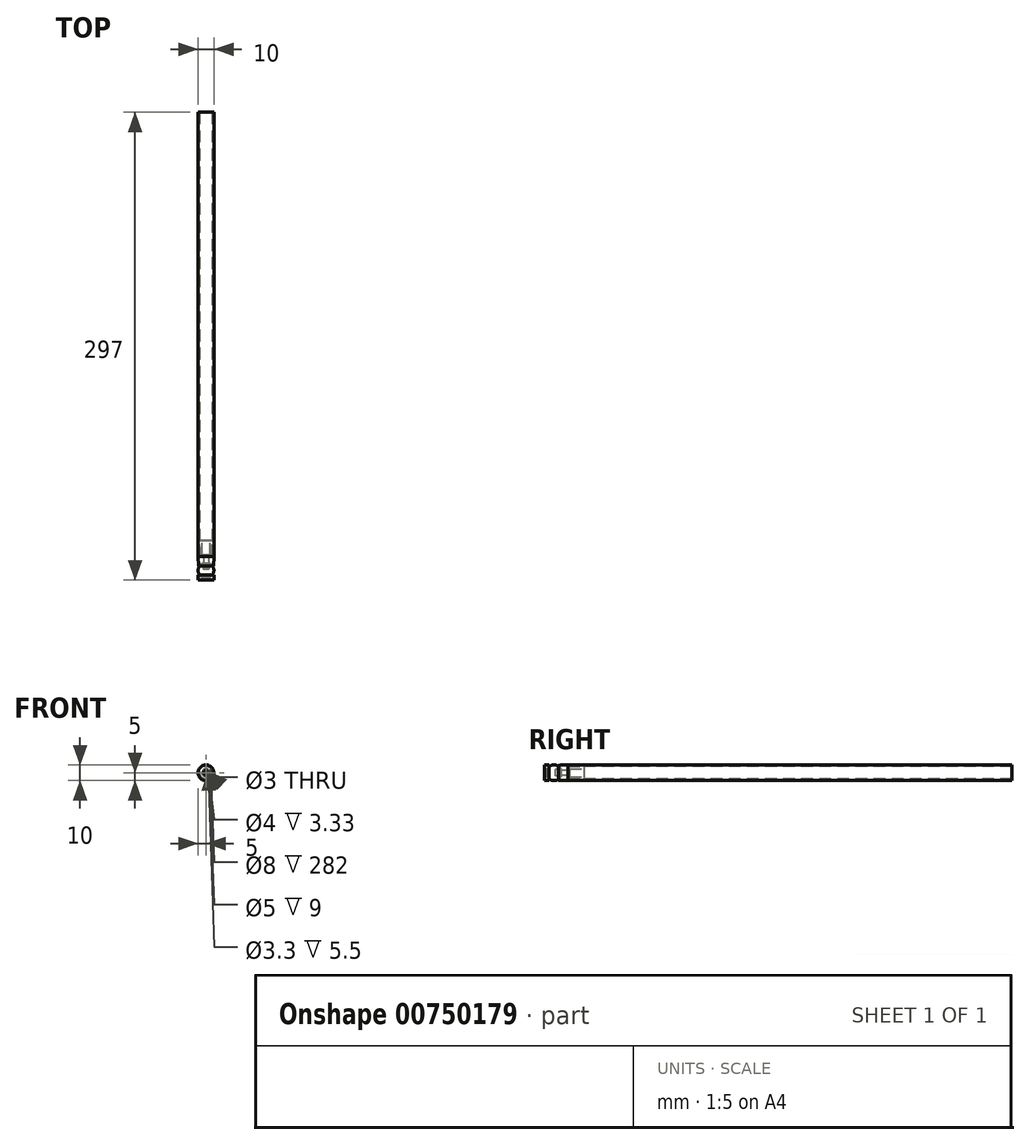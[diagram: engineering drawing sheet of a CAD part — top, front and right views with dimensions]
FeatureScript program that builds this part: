
annotation { "Feature Type Name" : "Feature", "Feature Type Description" : "" }
export const myFeature = defineFeature(function(context is Context, id is Id, definition is map)
    precondition{}
    {
        {
            var Q0;
            Q0=qCreatedBy(makeId("Top.planeOp"),FACE);
            var sketch = newSketch(context, id + "F0", { "sketchPlane" : qUnion([Q0])});
            skArc(sketch, "E0", {"start": v(0, -11.5) * mm, "mid": v(5, -6.5) * mm, "end": v(0, -1.5) * mm, "construction": true});
            skLineSegment(sketch, "E1.bottom", {"start": v(-6, 286) * mm, "end": v(-5, 286) * mm});
            skLineSegment(sketch, "E2", {"start": v(0, -11.5) * mm, "end": v(0, -6.5) * mm});
            skLineSegment(sketch, "E3", {"start": v(0, -6.5) * mm, "end": v(-5, -6.5) * mm, "construction": true});
            skLineSegment(sketch, "E4.MirrorCS", {"start": v(-5, -9.5) * mm, "end": v(-4, -9.5) * mm});
            skLineSegment(sketch, "E5.MirrorCS", {"start": v(-5, -12.5) * mm, "end": v(-5, -9.5) * mm});
            skLineSegment(sketch, "E6.MirrorCS", {"start": v(-5, -12.5) * mm, "end": v(-1.5, -12.5) * mm});
            skLineSegment(sketch, "E7.MirrorCS", {"start": v(-1.5, -12.5) * mm, "end": v(-1.5, -11.27) * mm});
            skLineSegment(sketch, "E8", {"start": v(-2, -2.17) * mm, "end": v(-2, -5.5) * mm});
            skLineSegment(sketch, "E9", {"start": v(-2, -5.5) * mm, "end": v(0, -5.5) * mm});
            skLineSegment(sketch, "E10", {"start": v(-2.5, -2.17) * mm, "end": v(-2, -2.17) * mm});
            skArc(sketch, "E11", {"start": v(0, -11.5) * mm, "mid": v(-4.83, -7.8) * mm, "end": v(-2.5, -2.17) * mm});
            skLineSegment(sketch, "E12", {"start": v(0, -6.5) * mm, "end": v(0, -5.5) * mm});
            skSolve(sketch);
        }
        {
            var Q0;
            Q0=qCreatedBy(makeId("Top.planeOp"),FACE);
            var sketch = newSketch(context, id + "F1", { "sketchPlane" : qUnion([Q0])});
            skLineSegment(sketch, "E13.bottom", {"start": v(-5, 2.5) * mm, "end": v(-4, 2.5) * mm});
            skLineSegment(sketch, "E13.top", {"start": v(-5, 284.5) * mm, "end": v(-4, 284.5) * mm});
            skLineSegment(sketch, "E13.left", {"start": v(-5, 2.5) * mm, "end": v(-5, 284.5) * mm});
            skLineSegment(sketch, "E13.right", {"start": v(-4, 2.5) * mm, "end": v(-4, 284.5) * mm});
            skSolve(sketch);
        }
        {
            var Q0;
            Q0=makeQuery(id+"F1.imprint","IMPRINT",FACE,{"disambiguationData":[TD([[makeQuery(id+"F1.imprint","IMPRINT",EDGE,{"derivedFrom":sQuery(id+"F1.wireOp",EDGE,"E13.bottom")}),1.0]])]});
            var Q1;
            Q1=sQuery(id+"F0.wireOp",EDGE,"E2");
            revolve(context, id + "F2", {"surfaceOperationType" : NewSurfaceOperationType.NEW, "entities" : qUnion([Q0]), "axis" : qUnion([Q1]), "revolveType" : RevolveType.FULL});
        }
        {
            var Q0;
            {var subQ0=sQuery(id+"F0.wireOp",EDGE,"E4.MirrorCS");Q0=makeQuery(id+"F0.imprint","IMPRINT",FACE,{"disambiguationData":[TD([[makeQuery(id+"F0.imprint","IMPRINT",EDGE,{"derivedFrom":subQ0}),-1.0]])]});}
            var Q1;
            Q1=sQuery(id+"F0.wireOp",EDGE,"E2");
            revolve(context, id + "F3", {"surfaceOperationType" : NewSurfaceOperationType.NEW, "entities" : qUnion([Q0]), "axis" : qUnion([Q1]), "revolveType" : RevolveType.FULL});
        }
        {
            var Q0;
            {var subQ1=sQuery(id+"F0.wireOp",EDGE,"E2");Q0=makeQuery(id+"F0.imprint","IMPRINT",FACE,{"disambiguationData":[TD([[makeQuery(id+"F0.imprint","IMPRINT",EDGE,{"derivedFrom":subQ1}),1.0]])]});}
            var Q1;
            Q1=sQuery(id+"F0.wireOp",EDGE,"E12");
            revolve(context, id + "F4", {"surfaceOperationType" : NewSurfaceOperationType.NEW, "entities" : qUnion([Q0]), "axis" : qUnion([Q1]), "revolveType" : RevolveType.FULL});
        }
        {
            var Q0;
            Q0=qCreatedBy(makeId("Top.planeOp"),FACE);
            var sketch = newSketch(context, id + "F5", { "sketchPlane" : qUnion([Q0])});
            skArc(sketch, "E14.0", {"start": v(0, -11.5) * mm, "mid": v(-4.87, -7.62) * mm, "end": v(-2.18, -2) * mm});
            skPoint(sketch, "E15", {"position": v(-5, 2.5) * mm});
            skPoint(sketch, "E16", {"position": v(-4, 2.5) * mm});
            skLineSegment(sketch, "E17", {"start": v(-4, 2.5) * mm, "end": v(-4, 12.5) * mm});
            skLineSegment(sketch, "E18", {"start": v(-4, 12.5) * mm, "end": v(-2.5, 12.5) * mm});
            skLineSegment(sketch, "E19", {"start": v(-2.5, 12.5) * mm, "end": v(-2.5, -0.5) * mm});
            skLineSegment(sketch, "E20", {"start": v(-4, 2.5) * mm, "end": v(-5, 2.5) * mm});
            skLineSegment(sketch, "E21", {"start": v(-2.5, -0.5) * mm, "end": v(0, -0.5) * mm});
            skLineSegment(sketch, "E22", {"start": v(0, -0.5) * mm, "end": v(0, -2) * mm});
            skLineSegment(sketch, "E23", {"start": v(0, -2) * mm, "end": v(-2.18, -2) * mm});
            skLineSegment(sketch, "E24", {"start": v(-4.8, -3.5) * mm, "end": v(-5, 2.5) * mm});
            skLineSegment(sketch, "E25", {"start": v(0, -0.5) * mm, "end": v(0, 3.5) * mm});
            skLineSegment(sketch, "E26", {"start": v(0, 3.5) * mm, "end": v(-2.5, 3.5) * mm});
            skLineSegment(sketch, "E27", {"start": v(-4, -3.5) * mm, "end": v(-4.8, -3.5) * mm});
            skLineSegment(sketch, "E28", {"start": v(-5, 2.5) * mm, "end": v(-5, 6.45) * mm});
            skLineSegment(sketch, "E29", {"start": v(-5, 6.45) * mm, "end": v(-5.8, 6.45) * mm});
            skArc(sketch, "E30", {"start": v(-5.8, 6.45) * mm, "mid": v(-5.55, 1.45) * mm, "end": v(-4.8, -3.5) * mm});
            skLineSegment(sketch, "E31", {"start": v(-5.8, 6.45) * mm, "end": v(-5.8, -7.35) * mm, "construction": true});
            skSolve(sketch);
        }
        {
            var Q0;
            Q0=makeQuery(id+"F5.imprint","IMPRINT",FACE,{"disambiguationData":[TD([[makeQuery(id+"F5.imprint","IMPRINT",EDGE,{"derivedFrom":sQuery(id+"F5.wireOp",EDGE,"E17")}),-1.0]])]});
            var Q1;
            {var subQ0=sQuery(id+"F5.wireOp",EDGE,"E21");Q1=makeQuery(id+"F5.imprint","IMPRINT",FACE,{"disambiguationData":[TD([[makeQuery(id+"F5.imprint","IMPRINT",EDGE,{"derivedFrom":subQ0}),1.0]])]});}
            var Q2;
            Q2=sQuery(id+"F5.wireOp",EDGE,"E22");
            revolve(context, id + "F6", {"surfaceOperationType" : NewSurfaceOperationType.NEW, "entities" : qUnion([Q0, Q1]), "axis" : qUnion([Q2]), "revolveType" : RevolveType.FULL});
        }
        {
            var Q0;
            Q0=makeQuery(id+"F6.opRevolve","SWEPT_FACE",FACE,{"disambiguationData":[OSD([sQuery(id+"F5.wireOp",EDGE,"E23")])]});
            var sketch = newSketch(context, id + "F7", { "sketchPlane" : qUnion([Q0])});
            skPoint(sketch, "E32", {"position": v(0, 0) * mm});
            skSolve(sketch);
        }
        {
            var Q0;
            Q0=sQuery(id+"F7.wireOp",VERTEX,"E32");
            var Q1;
            Q1=makeQuery(id+"F6.opRevolve","SWEPT_BODY",BODY,{"disambiguationData":[OSD([sQuery(id+"F5.wireOp",EDGE,"E14.0"),sQuery(id+"F5.wireOp",EDGE,"E17"),sQuery(id+"F5.wireOp",EDGE,"E18"),sQuery(id+"F5.wireOp",EDGE,"E19"),sQuery(id+"F5.wireOp",EDGE,"E20"),sQuery(id+"F5.wireOp",EDGE,"UlShArAt-zNfI-u8WC-8VMN-ArDZidGRxfLh"),sQuery(id+"F5.wireOp",EDGE,"E21"),sQuery(id+"F5.wireOp",EDGE,"E22"),sQuery(id+"F5.wireOp",EDGE,"E23")])]});
            hole(context, id + "F8", {"style" : HoleStyle.SIMPLE, "endStyle" : HoleEndStyle.BLIND, "standardTappedOrClearance" : lookupTablePath({ "standard" : "ISO", "engagement" : "75%", "pitch" : "0.7 mm", "size" : "M4", "type" : "Tapped" }), "standardBlindInLast" : lookupTablePath({ "standard" : "ISO", "engagement" : "75%", "pitch" : "0.7 mm", "size" : "M4", "type" : "Tapped" }), "holeDiameter" : 3.3 * mm, "majorDiameter" : 4 * mm, "showTappedDepth" : true, "holeDepth" : 8.6 * mm, "isTappedThrough" : true, "tappedDepth" : 6.5 * mm, "tapClearance" : 3, "locations" : qUnion([Q0]), "scope" : qUnion([Q1])});
        }
    });
